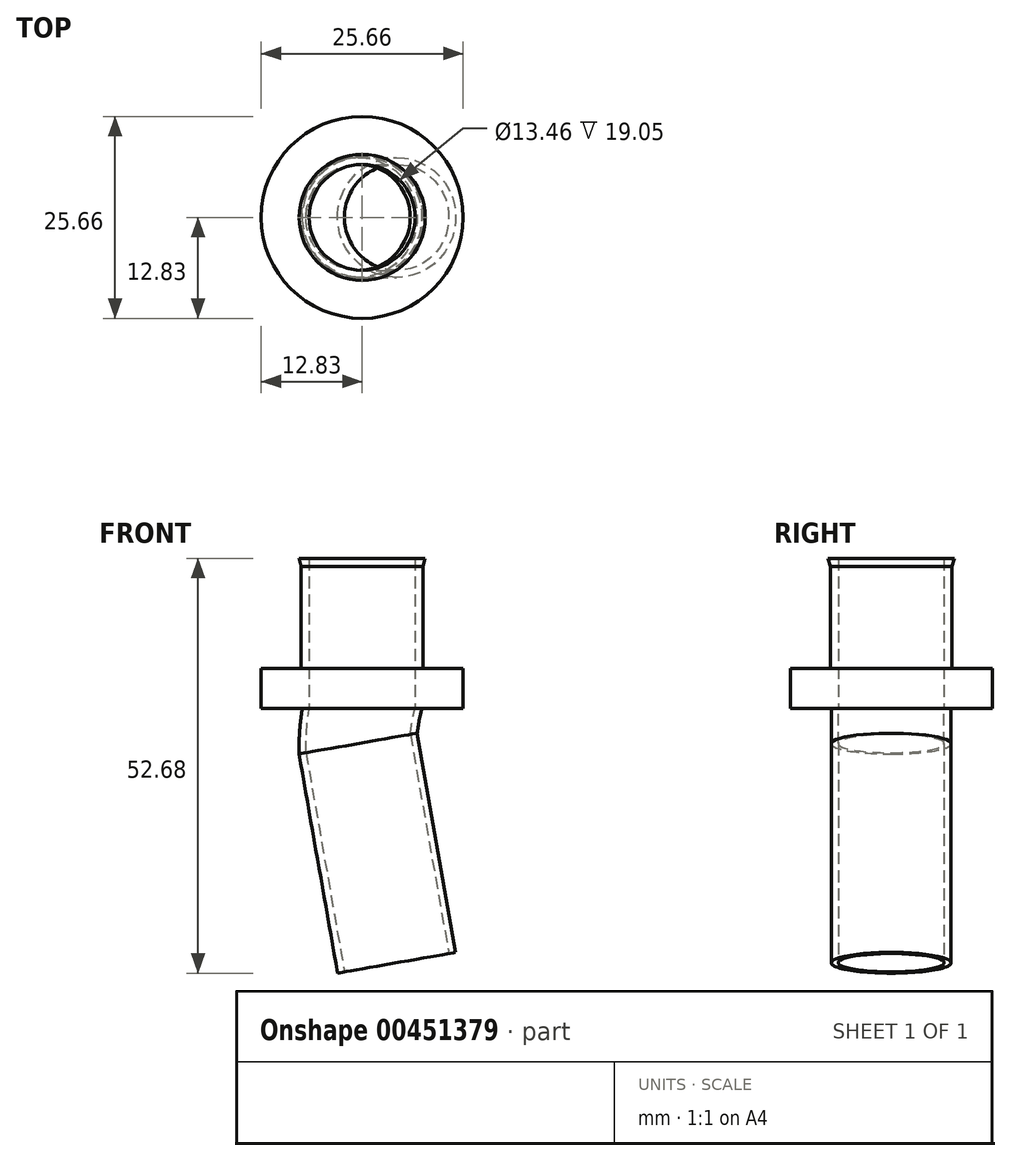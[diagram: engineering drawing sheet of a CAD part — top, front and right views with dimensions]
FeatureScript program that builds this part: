
annotation { "Feature Type Name" : "Feature", "Feature Type Description" : "" }
export const myFeature = defineFeature(function(context is Context, id is Id, definition is map)
    precondition{}
    {
        {
            var Q0;
            Q0=qCreatedBy(makeId("Front.planeOp"),FACE);
            var sketch = newSketch(context, id + "F0", { "sketchPlane" : qUnion([Q0])});
            skLineSegment(sketch, "E0", {"start": v(0, -10.24) * mm, "end": v(0, 36.32) * mm});
            skLineSegment(sketch, "E1.0", {"start": v(7.75, 0) * mm, "end": v(7.75, 12.95) * mm});
            skLineSegment(sketch, "E2.0", {"start": v(6.73, 0) * mm, "end": v(6.73, 12.95) * mm});
            skLineSegment(sketch, "E3", {"start": v(7.75, 0) * mm, "end": v(12.83, 0) * mm});
            skLineSegment(sketch, "E4", {"start": v(12.83, 0) * mm, "end": v(12.83, -5.08) * mm});
            skLineSegment(sketch, "E5", {"start": v(12.83, -5.08) * mm, "end": v(7.75, -5.08) * mm});
            skLineSegment(sketch, "E6", {"start": v(7.75, -5.08) * mm, "end": v(6.73, -5.08) * mm});
            skLineSegment(sketch, "E7", {"start": v(6.73, -5.08) * mm, "end": v(6.73, 0) * mm});
            skLineSegment(sketch, "E8", {"start": v(6.73, 12.95) * mm, "end": v(6.73, 13.97) * mm});
            skLineSegment(sketch, "E9", {"start": v(6.73, 13.97) * mm, "end": v(8, 13.97) * mm});
            skLineSegment(sketch, "E10", {"start": v(8, 13.97) * mm, "end": v(7.75, 12.95) * mm});
            skPoint(sketch, "E11", {"position": v(0, -5.08) * mm});
            skLineSegment(sketch, "E12", {"start": v(0.38, -14.64) * mm, "end": v(5.27, -42.48) * mm});
            skPoint(sketch, "E13.visualSharp", {"position": v(0, -12.46) * mm});
            skArc(sketch, "E13.filletArc", {"start": v(0, -10.24) * mm, "mid": v(0.1, -12.45) * mm, "end": v(0.38, -14.64) * mm});
            skSolve(sketch);
        }
        {
            var Q0;
            Q0=makeQuery(id+"F0.imprint","IMPRINT",FACE,{"disambiguationData":[TD([[makeQuery(id+"F0.imprint","IMPRINT",EDGE,{"derivedFrom":sQuery(id+"F0.wireOp",EDGE,"E1.0")}),1.0]])]});
            var Q1;
            Q1=sQuery(id+"F0.wireOp",EDGE,"E0");
            revolve(context, id + "F1", {"surfaceOperationType" : NewSurfaceOperationType.NEW, "entities" : qUnion([Q0]), "axis" : qUnion([Q1]), "revolveType" : RevolveType.FULL});
        }
        {
            var Q0;
            Q0=makeQuery(id+"F1.opRevolve","SWEPT_FACE",FACE,{"disambiguationData":[OSD([sQuery(id+"F0.wireOp",EDGE,"E5"),sQuery(id+"F0.wireOp",EDGE,"E6")])]});
            var sketch = newSketch(context, id + "F2", { "sketchPlane" : qUnion([Q0])});
            skCircle(sketch, "E14", {"center": v(0, 0) * mm, "radius": 7.62 * mm});
            skCircle(sketch, "E15.0", {"center": v(0, 0) * mm, "radius": 6.73 * mm});
            skLineSegment(sketch, "E16.0", {"start": v(0, 0) * mm, "end": v(0.38, 0) * mm});
            skLineSegment(sketch, "E17.0", {"start": v(0.38, 0) * mm, "end": v(5.27, 0) * mm});
            skSolve(sketch);
        }
        {
            var Q0;
            Q0=makeQuery(id+"F2.imprint","IMPRINT",FACE,{"disambiguationData":[TD([[makeQuery(id+"F2.imprint","IMPRINT",EDGE,{"derivedFrom":sQuery(id+"F2.wireOp",EDGE,"E14")}),1.0]])]});
            var Q1;
            Q1=sQuery(id+"F0.wireOp",EDGE,"E13.filletArc");
            var Q2;
            Q2=sQuery(id+"F0.wireOp",EDGE,"E12");
            sweep(context, id + "F3", {"operationType" : NewBodyOperationType.ADD, "profiles" : qUnion([Q0]), "path" : qUnion([Q1, Q2])});
        }
    });
